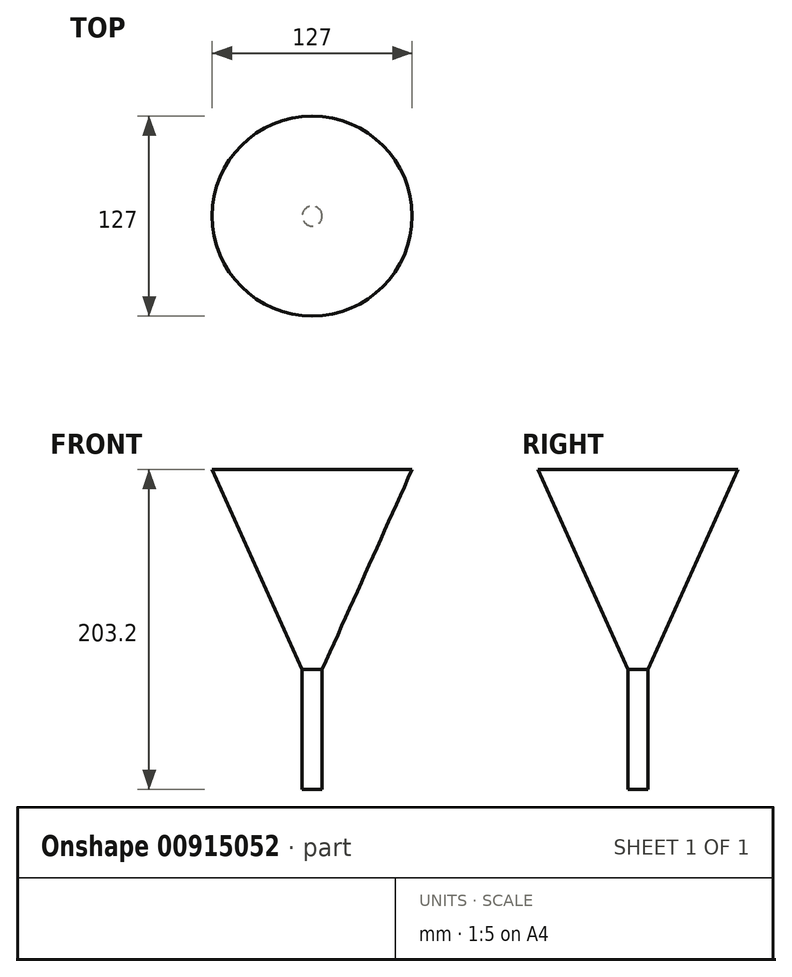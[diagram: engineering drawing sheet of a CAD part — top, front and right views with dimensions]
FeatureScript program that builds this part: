
annotation { "Feature Type Name" : "Feature", "Feature Type Description" : "" }
export const myFeature = defineFeature(function(context is Context, id is Id, definition is map)
    precondition{}
    {
        {
            var Q0;
            Q0=qCreatedBy(makeId("Top.planeOp"),FACE);
            cPlane(context, id + "F0", {"entities" : qUnion([Q0]), "cplaneType" : CPlaneType.OFFSET, "offset" : 76.2 * mm, "width" : 152.4 * mm, "height" : 152.4 * mm});
        }
        {
            var Q0;
            Q0=qCreatedBy(id+"F0.planeOp",FACE);
            cPlane(context, id + "F1", {"entities" : qUnion([Q0]), "cplaneType" : CPlaneType.OFFSET, "offset" : 127 * mm, "width" : 152.4 * mm, "height" : 152.4 * mm});
        }
        {
            var Q0;
            Q0=qCreatedBy(makeId("Top.planeOp"),FACE);
            var sketch = newSketch(context, id + "F2", { "sketchPlane" : qUnion([Q0])});
            skCircle(sketch, "E0", {"center": v(0, 0) * mm, "radius": 6.35 * mm});
            skSolve(sketch);
        }
        {
            var Q0;
            Q0=qCreatedBy(id+"F0.planeOp",FACE);
            var sketch = newSketch(context, id + "F3", { "sketchPlane" : qUnion([Q0])});
            skCircle(sketch, "E1", {"center": v(0, 0) * mm, "radius": 6.35 * mm});
            skSolve(sketch);
        }
        {
            var Q0;
            Q0=qCreatedBy(id+"F1.planeOp",FACE);
            var sketch = newSketch(context, id + "F4", { "sketchPlane" : qUnion([Q0])});
            skCircle(sketch, "E2", {"center": v(0, 0) * mm, "radius": 63.5 * mm});
            skSolve(sketch);
        }
        {
            var Q0;
            Q0=makeQuery(id+"F3.imprint","IMPRINT",FACE,{"disambiguationData":[TD([[makeQuery(id+"F3.imprint","IMPRINT",EDGE,{"derivedFrom":sQuery(id+"F3.wireOp",EDGE,"E1")}),1.0]])]});
            var Q1;
            Q1=makeQuery(id+"F4.imprint","IMPRINT",FACE,{"disambiguationData":[TD([[makeQuery(id+"F4.imprint","IMPRINT",EDGE,{"derivedFrom":sQuery(id+"F4.wireOp",EDGE,"E2")}),1.0]])]});
            loft(context, id + "F5", {"sheetProfilesArray" : [{ "sheetProfileEntities" : qUnion([Q0]) }, { "sheetProfileEntities" : qUnion([Q1]) }]});
        }
        {
            var Q0;
            Q0 = qSketchRegion(id + "F2", true);
            extrude(context, id + "F6", {"entities" : qUnion([Q0]), "operationType" : NewBodyOperationType.ADD, "depth" : 78.74 * mm, "offsetDistance" : 25.4 * mm});
        }
    });
